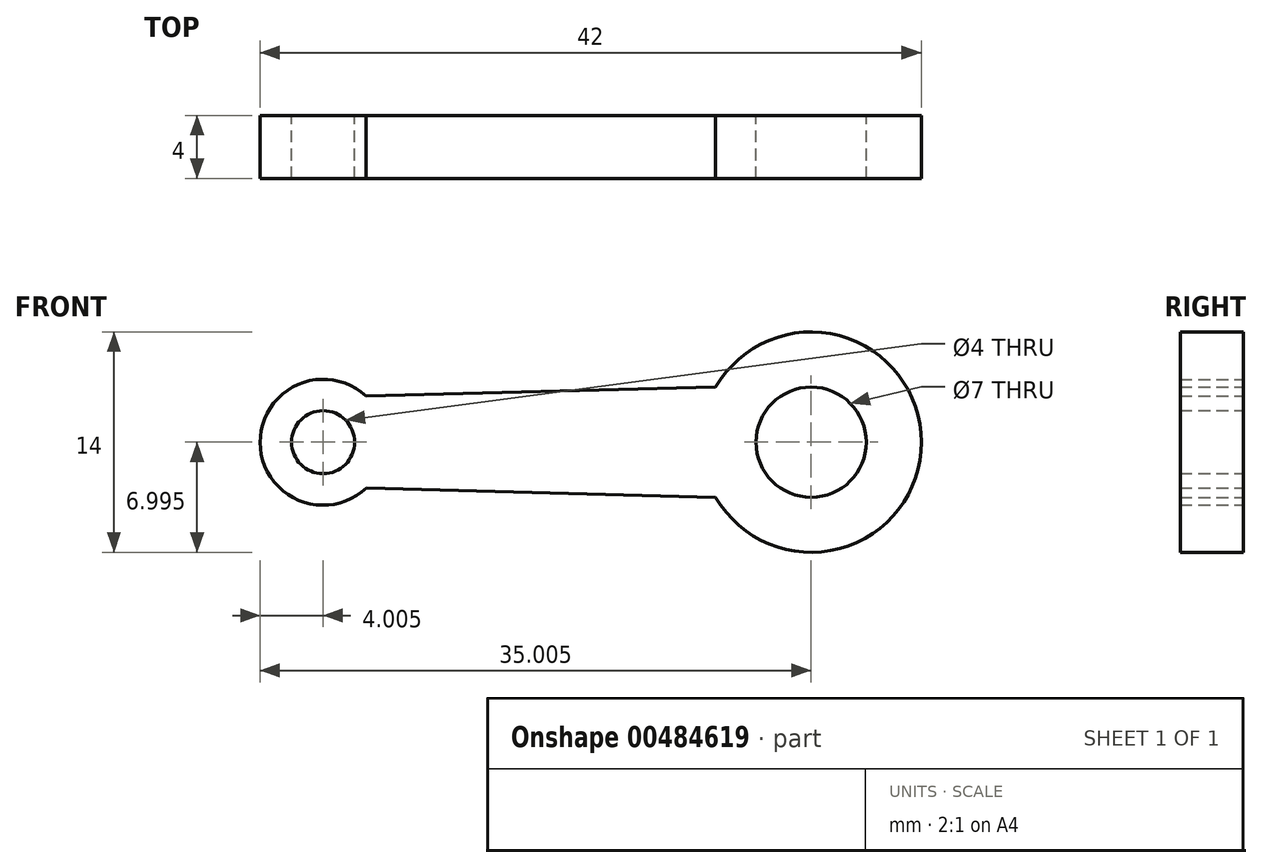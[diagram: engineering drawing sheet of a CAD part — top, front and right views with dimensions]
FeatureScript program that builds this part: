
annotation { "Feature Type Name" : "Feature", "Feature Type Description" : "" }
export const myFeature = defineFeature(function(context is Context, id is Id, definition is map)
    precondition{}
    {
        {
            var Q0;
            Q0=qCreatedBy(makeId("Front.planeOp"),FACE);
            var sketch = newSketch(context, id + "F0", { "sketchPlane" : qUnion([Q0])});
            skLineSegment(sketch, "E0", {"start": v(-87.56, 12.77) * mm, "end": v(-56.56, 12.77) * mm, "construction": true});
            skCircle(sketch, "E1", {"center": v(-56.56, 12.77) * mm, "radius": 7 * mm});
            skCircle(sketch, "E2", {"center": v(-87.56, 12.77) * mm, "radius": 4 * mm});
            skCircle(sketch, "E3", {"center": v(-87.56, 12.77) * mm, "radius": 2 * mm});
            skCircle(sketch, "E4", {"center": v(-56.56, 12.77) * mm, "radius": 3.5 * mm});
            skLineSegment(sketch, "E5", {"start": v(-83.55, 15.77) * mm, "end": v(-83.55, 9.77) * mm, "construction": true});
            skLineSegment(sketch, "E6", {"start": v(-63.6, 16.27) * mm, "end": v(-63.6, 9.27) * mm, "construction": true});
            skLineSegment(sketch, "E7", {"start": v(-84.84, 15.7) * mm, "end": v(-62.62, 16.26) * mm});
            skLineSegment(sketch, "E8", {"start": v(-84.8, 9.86) * mm, "end": v(-62.62, 9.27) * mm});
            skSolve(sketch);
        }
        {
            var Q0;
            {var subQ0=sQuery(id+"F0.wireOp",EDGE,"E7");Q0=makeQuery(id+"F0.imprint","IMPRINT",FACE,{"disambiguationData":[TD([[makeQuery(id+"F0.imprint","IMPRINT",EDGE,{"derivedFrom":subQ0}),-1.0]])]});}
            var Q1;
            Q1=makeQuery(id+"F0.imprint","IMPRINT",FACE,{"disambiguationData":[TD([[makeQuery(id+"F0.imprint","IMPRINT",EDGE,{"derivedFrom":sQuery(id+"F0.wireOp",EDGE,"E3")}),-1.0]])]});
            var Q2;
            Q2=makeQuery(id+"F0.imprint","IMPRINT",FACE,{"disambiguationData":[TD([[makeQuery(id+"F0.imprint","IMPRINT",EDGE,{"derivedFrom":sQuery(id+"F0.wireOp",EDGE,"E4")}),-1.0]])]});
            extrude(context, id + "F1", {"entities" : qUnion([Q0, Q1, Q2]), "depth" : 4 * mm});
        }
    });
